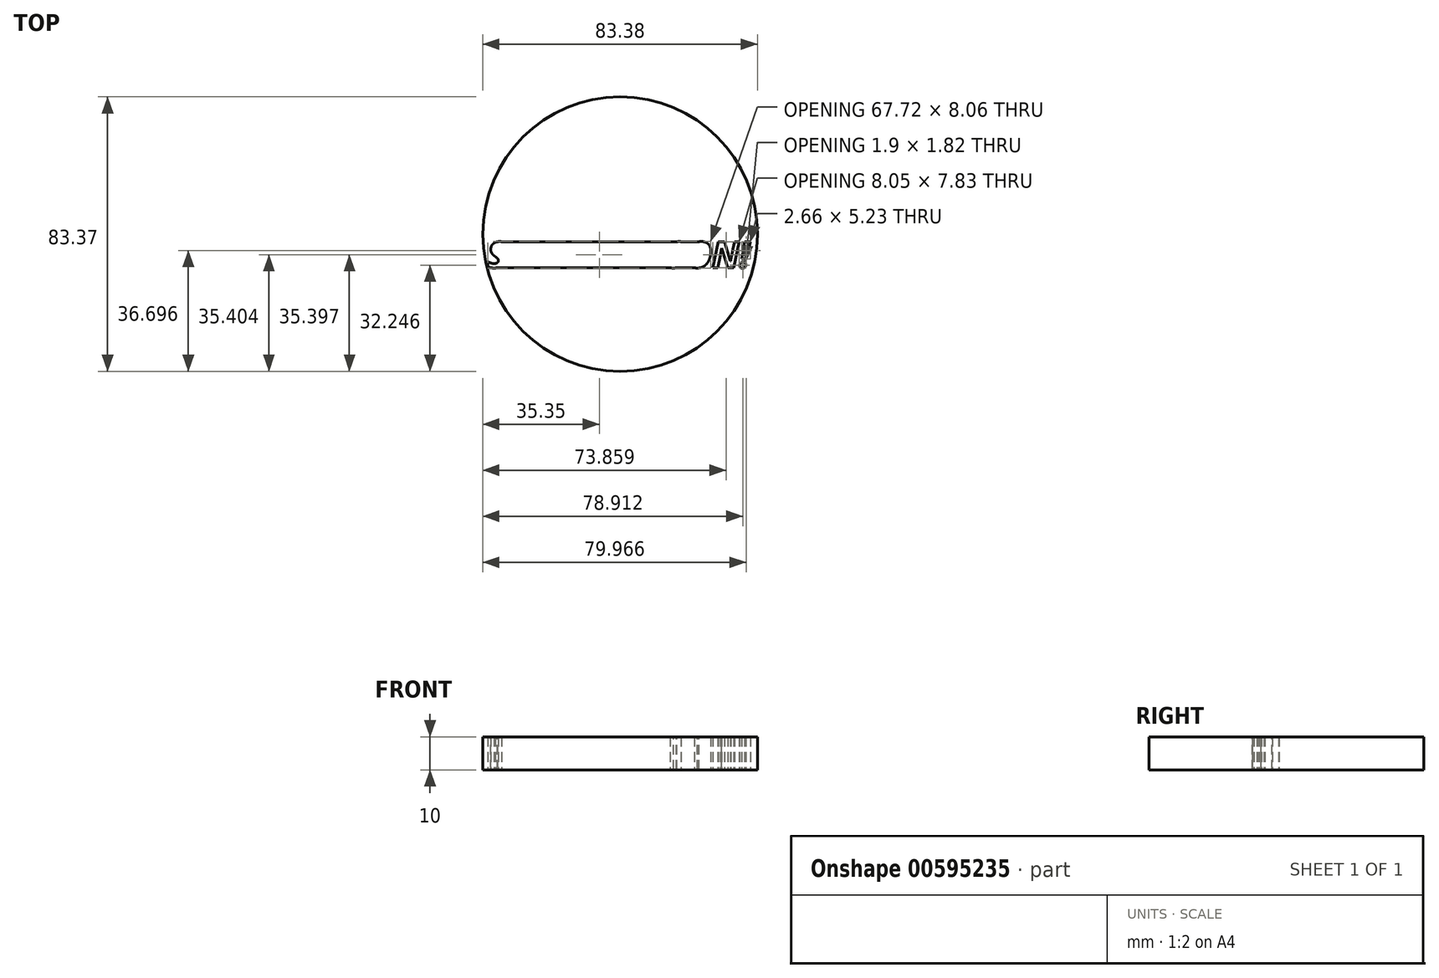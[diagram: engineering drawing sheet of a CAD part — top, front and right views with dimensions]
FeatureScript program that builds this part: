
annotation { "Feature Type Name" : "Feature", "Feature Type Description" : "" }
export const myFeature = defineFeature(function(context is Context, id is Id, definition is map)
    precondition{}
    {
        {
            var Q0;
            Q0=qCreatedBy(makeId("Top.planeOp"),FACE);
            var sketch = newSketch(context, id + "F0", { "sketchPlane" : qUnion([Q0])});
            skCircle(sketch, "E0", {"center": v(0, 2.3) * mm, "radius": 41.69 * mm});
            skLineSegment(sketch, "E1.bottom", {"start": v(40.42, 0) * mm, "end": v(-40.42, 0) * mm});
            skLineSegment(sketch, "E1.top", {"start": v(40.42, -7.9) * mm, "end": v(-40.42, -7.9) * mm});
            skLineSegment(sketch, "E1.left", {"start": v(40.42, 0) * mm, "end": v(40.42, -7.9) * mm});
            skLineSegment(sketch, "E1.right", {"start": v(-40.42, 0) * mm, "end": v(-40.42, -7.9) * mm});
            skPoint(sketch, "E1.middle", {"position": v(0, -3.95) * mm});
            skText(sketch, "E2", { "text": "SHEA ADDISON!", "fontName": "OpenSans-BoldItalic.ttf"});
            const initialGuessF0  = {"E2": [-0.04042, -0.0079, 1, 0, 0.0079]};
            skSetInitialGuess(sketch, initialGuessF0);
            skSolve(sketch);
        }
        {
            var Q0;
            Q0 = qSketchRegion(id + "F0", true);
            extrude(context, id + "F1", {"entities" : qUnion([Q0]), "depth" : 10 * mm, "offsetDistance" : 25 * mm});
        }
    });
